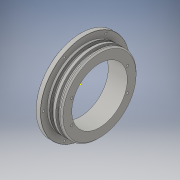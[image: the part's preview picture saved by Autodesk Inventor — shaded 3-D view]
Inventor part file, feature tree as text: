
AUTODESK INVENTOR PART (.ipt)
format: ipt  version: 2016 (Build 200138000, 138)  size: 635,904 bytes
history: native  units: in
note: dims shown in document units (in); Inventor stores cm internally (conversion verified against a paired STEP export)
features: sketch x5, extrude x3, chamfer x2, revolve x1, hole x1
ambient origin geometry x8: Origin, YZ Plane, XZ Plane, XY Plane, X Axis, Y Axis, Z Axis, Center Point
bodies: Solid1 (feature_tree)
feature tree (12):
  revolve  "Revolution1"  [1 undecoded]
  extrude  "Extrusion1"  Depth=0.13in
  extrude  "Extrusion2"  Depth=0.24in
  chamfer  "Chamfer1"  Distance=0.24in
  hole  "Hole1"  [1 undecoded]
  chamfer  "Chamfer2"  Distance=0.125in
  sketch  "Sketch8"  dims[d22=0.139in d23=0.0in d32=0.07in d33=0.125in d34=45.0deg]
  extrude  "Extrusion4"  Depth=0.995in
  sketch  "Sketch2"  dims[d2=0.175in d3=0.14in]
  sketch  "Sketch3"  dims[d4=0.175in d5=0.13in]
  sketch  "Sketch5"  dims[d8=90.0deg d10=4.65in d11=0.24in d12=0.0in]
  sketch  "Sketch9"  dims[d38=0.5in d42=0.125in d43=4.35in d44=2.3622in d46=360.0deg d48=0.1181in d49=0.75in d50=0.375in d51=0.25in d52=0.5635in d53=1.0in d54=0.8108in d55=0.01in d56=0.125in d57=45.0deg d62=3.819in d65=0.15in d66=0.15in d67=0.15in d68=0.055in d71=0.755in d72=1.68in d73=0.3in d74=0.3in d78=0.1181in d79=0.1181in d83=0.1181in d84=0.1181in d85=0.995in d86=0.0in]
note: 2 required parameter values undecoded (feature->parameter linkage not recoverable at this tier; creation-order binding heuristic only, values carry confidence <= 0.55)